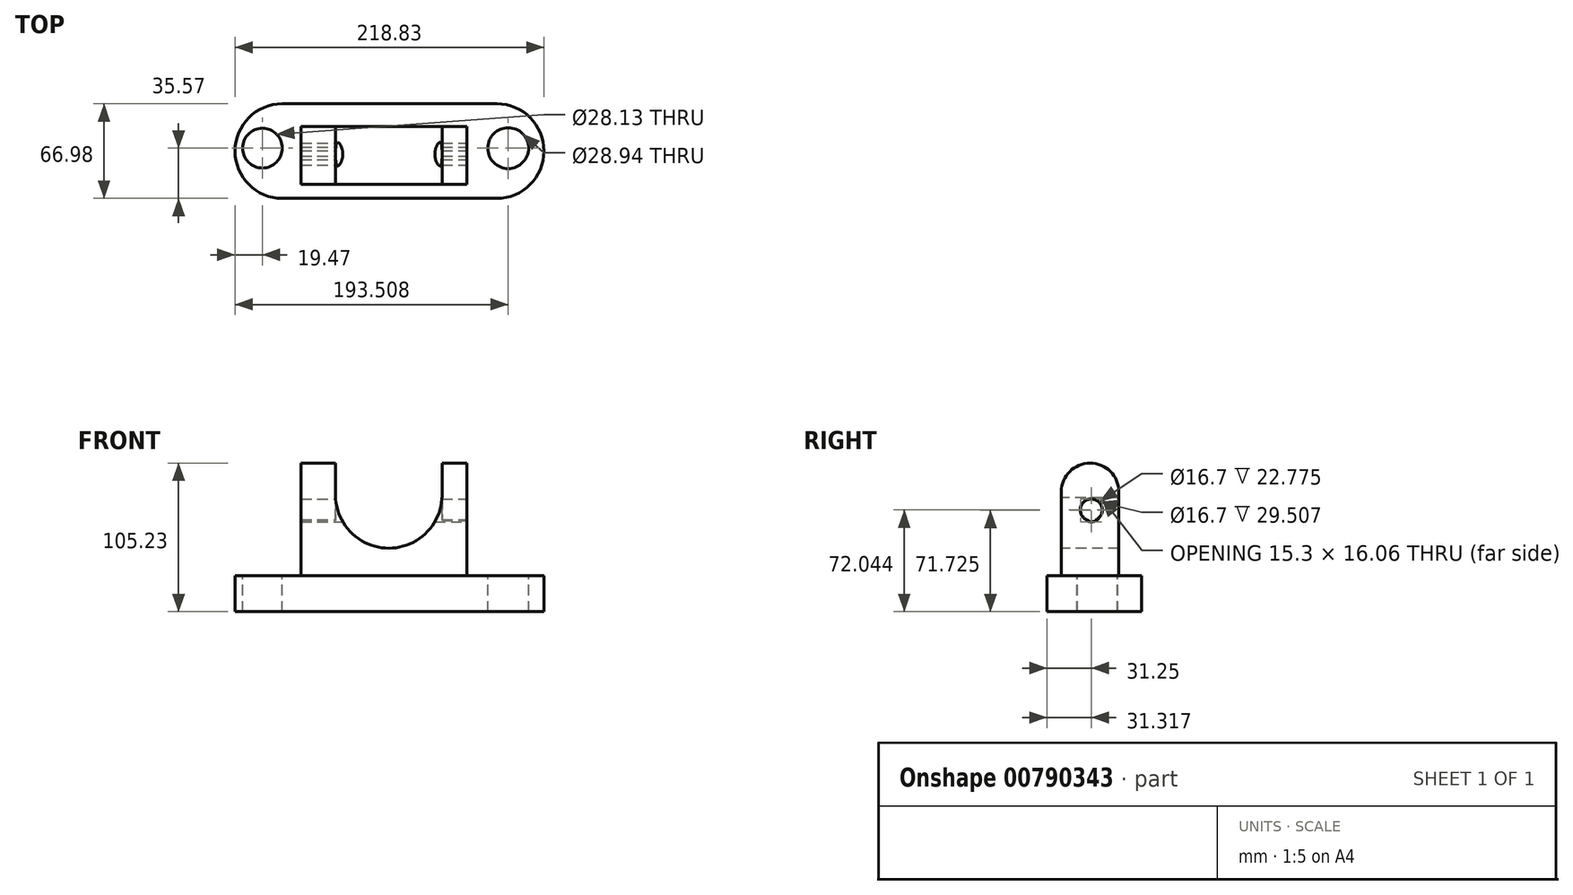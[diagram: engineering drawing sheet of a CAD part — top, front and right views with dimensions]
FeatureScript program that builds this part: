
annotation { "Feature Type Name" : "Feature", "Feature Type Description" : "" }
export const myFeature = defineFeature(function(context is Context, id is Id, definition is map)
    precondition{}
    {
        {
            var Q0;
            Q0=qCreatedBy(makeId("Top.planeOp"),FACE);
            var sketch = newSketch(context, id + "F0", { "sketchPlane" : qUnion([Q0])});
            skLineSegment(sketch, "E0.bottom", {"start": v(-75.8, -35.57) * mm, "end": v(76.05, -35.57) * mm});
            skLineSegment(sketch, "E0.top", {"start": v(-75.8, 31.4) * mm, "end": v(76.05, 31.4) * mm});
            skLineSegment(sketch, "E0.left", {"start": v(-75.8, -35.57) * mm, "end": v(-75.8, 31.4) * mm});
            skLineSegment(sketch, "E0.right", {"start": v(76.05, -35.57) * mm, "end": v(76.05, 31.4) * mm});
            skArc(sketch, "E1", {"start": v(-75.8, 31.4) * mm, "mid": v(-109.3, -2.08) * mm, "end": v(-75.8, -35.57) * mm});
            skArc(sketch, "E2", {"start": v(76.05, -35.57) * mm, "mid": v(109.54, -2.08) * mm, "end": v(76.05, 31.4) * mm});
            skSolve(sketch);
        }
        {
            var Q0;
            Q0=makeQuery(id+"F0.imprint","IMPRINT",FACE,{"disambiguationData":[TD([[makeQuery(id+"F0.imprint","IMPRINT",EDGE,{"derivedFrom":sQuery(id+"F0.wireOp",EDGE,"E0.bottom")}),1.0]])]});
            var Q1;
            Q1=makeQuery(id+"F0.imprint","IMPRINT",FACE,{"disambiguationData":[TD([[makeQuery(id+"F0.imprint","IMPRINT",EDGE,{"derivedFrom":sQuery(id+"F0.wireOp",EDGE,"E0.left")}),1.0]])]});
            var Q2;
            Q2=makeQuery(id+"F0.imprint","IMPRINT",FACE,{"disambiguationData":[TD([[makeQuery(id+"F0.imprint","IMPRINT",EDGE,{"derivedFrom":sQuery(id+"F0.wireOp",EDGE,"E0.right")}),-1.0]])]});
            extrude(context, id + "F1", {"entities" : qUnion([Q0, Q1, Q2]), "depth" : 25.4 * mm, "offsetDistance" : 25.4 * mm});
        }
        {
            var Q0;
            Q0=makeQuery(id+"F1.opExtrude","CAP_FACE",FACE,{"disambiguationData":[OSD([sQuery(id+"F0.wireOp",EDGE,"E0.bottom"),sQuery(id+"F0.wireOp",EDGE,"E0.top"),sQuery(id+"F0.wireOp",EDGE,"E1"),sQuery(id+"F0.wireOp",EDGE,"E2")])],"isStart":false});
            var sketch = newSketch(context, id + "F2", { "sketchPlane" : qUnion([Q0])});
            skCircle(sketch, "E3", {"center": v(-89.82, 0) * mm, "radius": 14.07 * mm});
            skCircle(sketch, "E4", {"center": v(84.22, 0) * mm, "radius": 14.47 * mm});
            skSolve(sketch);
        }
        {
            var Q0;
            Q0=makeQuery(id+"F2.imprint","IMPRINT",FACE,{"disambiguationData":[TD([[makeQuery(id+"F2.imprint","IMPRINT",EDGE,{"derivedFrom":sQuery(id+"F2.wireOp",EDGE,"E3")}),1.0]])]});
            extrude(context, id + "F3", {"entities" : qUnion([Q0]), "operationType" : NewBodyOperationType.REMOVE, "oppositeDirection" : true, "depth" : 49.53 * mm, "offsetDistance" : 25.4 * mm});
        }
        {
            var Q0;
            Q0=makeQuery(id+"F2.imprint","IMPRINT",FACE,{"disambiguationData":[TD([[makeQuery(id+"F2.imprint","IMPRINT",EDGE,{"derivedFrom":sQuery(id+"F2.wireOp",EDGE,"E4")}),1.0]])]});
            extrude(context, id + "F4", {"entities" : qUnion([Q0]), "operationType" : NewBodyOperationType.REMOVE, "oppositeDirection" : true, "depth" : 55.88 * mm, "offsetDistance" : 25.4 * mm});
        }
        {
            var Q0;
            Q0=makeQuery(id+"F1.opExtrude","CAP_FACE",FACE,{"disambiguationData":[OSD([sQuery(id+"F0.wireOp",EDGE,"E0.bottom"),sQuery(id+"F0.wireOp",EDGE,"E0.top"),sQuery(id+"F0.wireOp",EDGE,"E1"),sQuery(id+"F0.wireOp",EDGE,"E2")])],"isStart":false});
            var sketch = newSketch(context, id + "F5", { "sketchPlane" : qUnion([Q0])});
            skLineSegment(sketch, "E5.bottom", {"start": v(-62.5, 15.28) * mm, "end": v(55.02, 15.28) * mm});
            skLineSegment(sketch, "E5.top", {"start": v(-62.5, -25.5) * mm, "end": v(55.02, -25.5) * mm});
            skLineSegment(sketch, "E5.left", {"start": v(-62.5, 15.28) * mm, "end": v(-62.5, -25.5) * mm});
            skLineSegment(sketch, "E5.right", {"start": v(55.02, 15.28) * mm, "end": v(55.02, -25.5) * mm});
            skSolve(sketch);
        }
        {
            var Q0;
            Q0=makeQuery(id+"F5.imprint","IMPRINT",FACE,{"disambiguationData":[TD([[makeQuery(id+"F5.imprint","IMPRINT",EDGE,{"derivedFrom":sQuery(id+"F5.wireOp",EDGE,"E5.bottom")}),-1.0]])]});
            extrude(context, id + "F6", {"entities" : qUnion([Q0]), "operationType" : NewBodyOperationType.ADD, "depth" : 59.44 * mm, "offsetDistance" : 25.4 * mm});
        }
        {
            var Q0;
            Q0=makeQuery(id+"F6.opExtrude","SWEPT_FACE",FACE,{"disambiguationData":[OSD([sQuery(id+"F5.wireOp",EDGE,"E5.top")])]});
            var sketch = newSketch(context, id + "F7", { "sketchPlane" : qUnion([Q0])});
            skArc(sketch, "E6", {"start": v(-38.08, 84.84) * mm, "mid": v(-0.37, 44.97) * mm, "end": v(37.35, 84.84) * mm});
            skSolve(sketch);
        }
        {
            var Q0;
            {var subQ0=sQuery(id+"F7.wireOp",EDGE,"E6");Q0=makeQuery(id+"F7.imprint","IMPRINT",FACE,{"disambiguationData":[TD([[makeQuery(id+"F7.imprint","IMPRINT",EDGE,{"derivedFrom":subQ0}),1.0]])]});}
            extrude(context, id + "F8", {"entities" : qUnion([Q0]), "operationType" : NewBodyOperationType.REMOVE, "oppositeDirection" : true, "depth" : 88.65 * mm, "offsetDistance" : 25.4 * mm});
        }
        {
            var Q0;
            Q0=makeQuery(id+"F6.opExtrude","SWEPT_FACE",FACE,{"disambiguationData":[OSD([sQuery(id+"F5.wireOp",EDGE,"E5.right")])]});
            var sketch = newSketch(context, id + "F9", { "sketchPlane" : qUnion([Q0])});
            skCircle(sketch, "E7", {"center": v(-4.25, 72.04) * mm, "radius": 8.35 * mm});
            skSolve(sketch);
        }
        {
            var Q0;
            Q0=makeQuery(id+"F9.imprint","IMPRINT",FACE,{"disambiguationData":[TD([[makeQuery(id+"F9.imprint","IMPRINT",EDGE,{"derivedFrom":sQuery(id+"F9.wireOp",EDGE,"E7")}),1.0]])]});
            extrude(context, id + "F10", {"entities" : qUnion([Q0]), "operationType" : NewBodyOperationType.REMOVE, "oppositeDirection" : true, "depth" : 232.16 * mm, "offsetDistance" : 25.4 * mm});
        }
        {
            var Q0;
            {var subQ0=sQuery(id+"F5.wireOp",EDGE,"E5.bottom");var subQ1=sQuery(id+"F5.wireOp",EDGE,"E5.right");var subQ2=sQuery(id+"F5.wireOp",EDGE,"E5.top");Q0=makeQuery(id+"F8.boolean.opBoolean","SPLIT",FACE,{"disambiguationData":[TD([makeQuery(id+"F6.opExtrude","SWEPT_FACE",FACE,{"disambiguationData":[OSD([subQ1])]})])],"derivedFrom":makeQuery(id+"F6.opExtrude","CAP_FACE",FACE,{"disambiguationData":[OSD([subQ0,subQ2,sQuery(id+"F5.wireOp",EDGE,"E5.left"),subQ1])],"isStart":false})});}
            var sketch = newSketch(context, id + "F11", { "sketchPlane" : qUnion([Q0])});
            skLineSegment(sketch, "E8", {"start": v(55.02, -5.1) * mm, "end": v(37.35, -5.1) * mm});
            skSolve(sketch);
        }
        {
            var Q0;
            {var subQ0=sQuery(id+"F5.wireOp",EDGE,"E5.bottom");var subQ1=sQuery(id+"F5.wireOp",EDGE,"E5.top");var subQ2=sQuery(id+"F5.wireOp",EDGE,"E5.left");Q0=makeQuery(id+"F8.boolean.opBoolean","SPLIT",FACE,{"disambiguationData":[TD([makeQuery(id+"F6.opExtrude","SWEPT_FACE",FACE,{"disambiguationData":[OSD([subQ2])]})])],"derivedFrom":makeQuery(id+"F6.opExtrude","CAP_FACE",FACE,{"disambiguationData":[OSD([subQ0,subQ1,subQ2,sQuery(id+"F5.wireOp",EDGE,"E5.right")])],"isStart":false})});}
            var sketch = newSketch(context, id + "F12", { "sketchPlane" : qUnion([Q0])});
            skLineSegment(sketch, "E9", {"start": v(-38.08, -5.1) * mm, "end": v(-62.5, -5.1) * mm});
            skSolve(sketch);
        }
        {
            var Q0;
            {var subQ0=sQuery(id+"F12.wireOp",EDGE,"E9");Q0=makeQuery(id+"F12.imprint","IMPRINT",FACE,{"disambiguationData":[TD([[makeQuery(id+"F12.imprint","IMPRINT",EDGE,{"derivedFrom":subQ0}),1.0]])]});}
            var Q1;
            Q1=sQuery(id+"F12.wireOp",EDGE,"E9");
            revolve(context, id + "F13", {"operationType" : NewBodyOperationType.ADD, "surfaceOperationType" : NewSurfaceOperationType.NEW, "entities" : qUnion([Q0]), "axis" : qUnion([Q1]), "revolveType" : RevolveType.FULL});
        }
        {
            var Q0;
            {var subQ0=sQuery(id+"F11.wireOp",EDGE,"E8");Q0=makeQuery(id+"F11.imprint","IMPRINT",FACE,{"disambiguationData":[TD([[makeQuery(id+"F11.imprint","IMPRINT",EDGE,{"derivedFrom":subQ0}),1.0]])]});}
            var Q1;
            Q1=sQuery(id+"F11.wireOp",EDGE,"E8");
            revolve(context, id + "F14", {"operationType" : NewBodyOperationType.ADD, "surfaceOperationType" : NewSurfaceOperationType.NEW, "entities" : qUnion([Q0]), "axis" : qUnion([Q1]), "revolveType" : RevolveType.FULL});
        }
        {
            var Q0;
            {var subQ0=sQuery(id+"F5.wireOp",EDGE,"E5.right");Q0=makeQuery(id+"F14.boolean.opBoolean","MERGE",FACE,{"derivedFrom":[makeQuery(id+"F6.opExtrude","SWEPT_FACE",FACE,{"disambiguationData":[OSD([subQ0])]}),makeQuery(id+"F14.opRevolve","SWEPT_FACE",FACE,{"disambiguationData":[OSD([subQ0])]})]});}
            var sketch = newSketch(context, id + "F15", { "sketchPlane" : qUnion([Q0])});
            skCircle(sketch, "E10", {"center": v(-4.25, 72.04) * mm, "radius": 7.73 * mm});
            skSolve(sketch);
        }
        {
            var Q0;
            {var subQ0=sQuery(id+"F15.wireOp",EDGE,"E10");var subQ1=sQuery(id+"F5.wireOp",EDGE,"E5.right");var subQ2=makeQuery(id+"F6.opExtrude","SWEPT_FACE",FACE,{"disambiguationData":[OSD([subQ1])]});var subQ3=sQuery(id+"F5.wireOp",EDGE,"E5.top");var subQ4=makeQuery(id+"F14.boolean.opBoolean","SPLIT",EDGE,{"disambiguationData":[TD([makeQuery(id+"F10.boolean.opBoolean","COPY",FACE,{"disambiguationData":[TD([subQ2])],"derivedFrom":makeQuery(id+"F10.opExtrude","SWEPT_FACE",FACE,{"disambiguationData":[OSD([sQuery(id+"F9.wireOp",EDGE,"E7")])]})})])],"derivedFrom":makeQuery(id+"F14.opRevolve","SWEPT_EDGE",EDGE,{"disambiguationData":[OSD([subQ3,subQ1])]})});var subQ5=makeQuery(id+"F15.imprint","INTERSECT",VERTEX,{"disambiguationData":[OD(0.0)],"derivedFrom":[subQ4,subQ0]});Q0=makeQuery(id+"F15.imprint","IMPRINT",FACE,{"disambiguationData":[TD([[makeQuery(id+"F15.imprint","IMPRINT",EDGE,{"disambiguationData":[TD([[subQ5,1.0]])],"derivedFrom":subQ0}),1.0]])]});}
            extrude(context, id + "F16", {"entities" : qUnion([Q0]), "operationType" : NewBodyOperationType.REMOVE, "oppositeDirection" : true, "depth" : 151.38 * mm, "offsetDistance" : 25.4 * mm});
        }
    });
